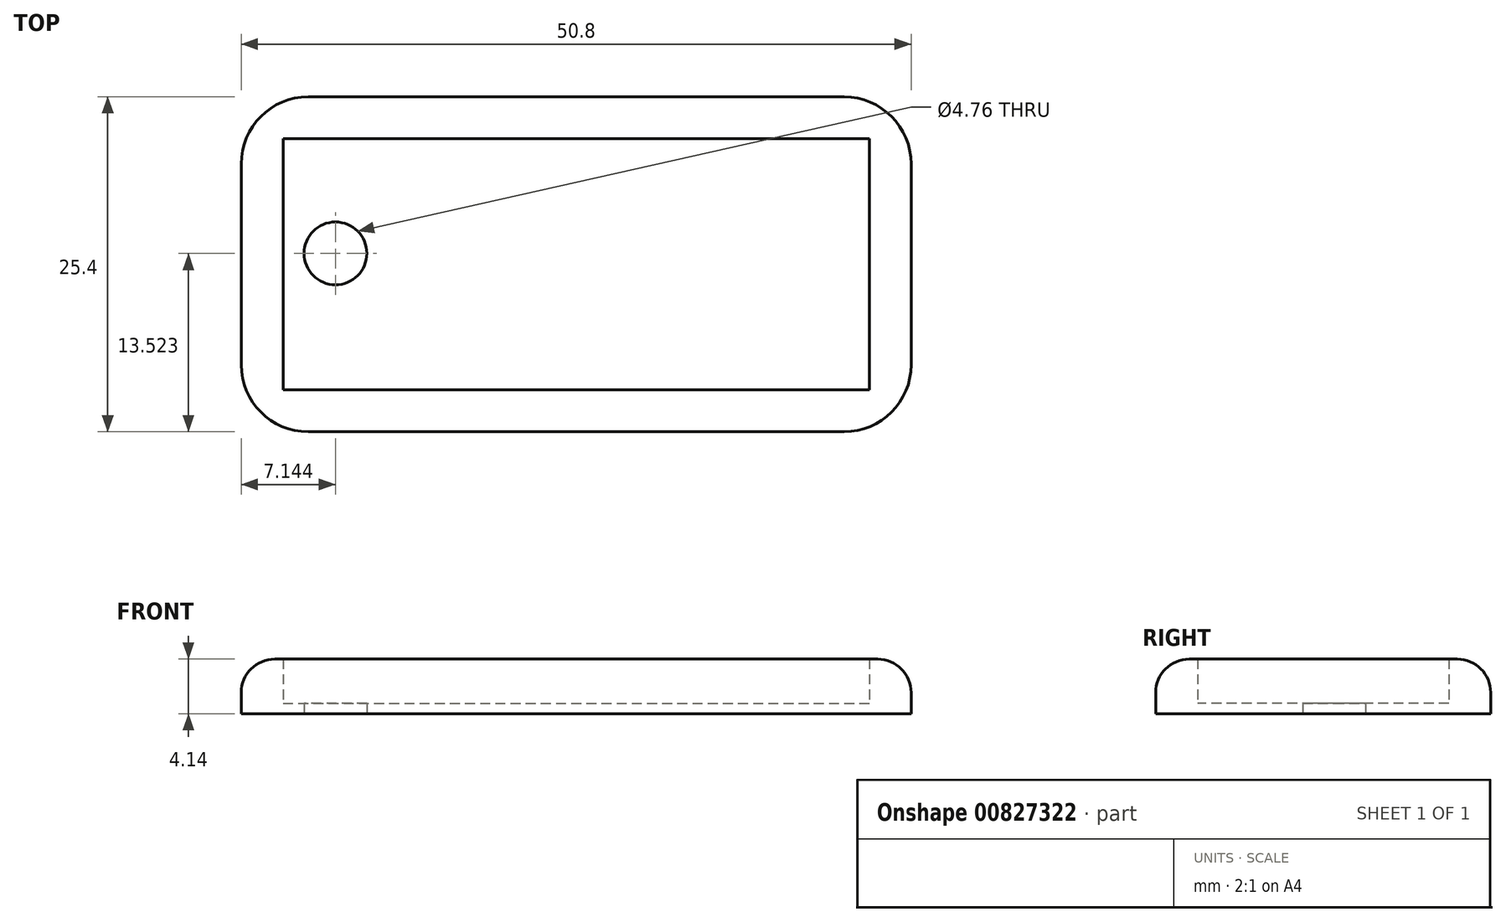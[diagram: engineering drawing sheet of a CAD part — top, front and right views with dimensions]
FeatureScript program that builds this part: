
annotation { "Feature Type Name" : "Feature", "Feature Type Description" : "" }
export const myFeature = defineFeature(function(context is Context, id is Id, definition is map)
    precondition{}
    {
        {
            var Q0;
            Q0=qCreatedBy(makeId("Top.planeOp"),FACE);
            var sketch = newSketch(context, id + "F0", { "sketchPlane" : qUnion([Q0])});
            skLineSegment(sketch, "E0.bottom", {"start": v(0, 0) * mm, "end": v(0, 0) * mm});
            skLineSegment(sketch, "E0.top", {"start": v(0, 23.75) * mm, "end": v(0, 23.75) * mm});
            skLineSegment(sketch, "E0.left", {"start": v(0, 0) * mm, "end": v(0, 23.75) * mm});
            skLineSegment(sketch, "E0.right", {"start": v(0, 0) * mm, "end": v(0, 23.75) * mm});
            skLineSegment(sketch, "E1.bottom", {"start": v(0, 23.75) * mm, "end": v(50.8, 23.75) * mm});
            skLineSegment(sketch, "E1.top", {"start": v(0, -1.65) * mm, "end": v(50.8, -1.65) * mm});
            skLineSegment(sketch, "E1.left", {"start": v(0, 23.75) * mm, "end": v(0, -1.65) * mm});
            skLineSegment(sketch, "E1.right", {"start": v(50.8, 23.75) * mm, "end": v(50.8, -1.65) * mm});
            skCircle(sketch, "E2", {"center": v(7.14, 11.87) * mm, "radius": 2.38 * mm});
            skPoint(sketch, "E2.centerSnap0", {"position": v(0, 11.87) * mm});
            skLineSegment(sketch, "E3.bottom", {"start": v(3.18, 20.57) * mm, "end": v(47.63, 20.57) * mm});
            skLineSegment(sketch, "E3.top", {"start": v(3.18, 1.52) * mm, "end": v(47.63, 1.52) * mm});
            skLineSegment(sketch, "E3.left", {"start": v(3.17, 20.57) * mm, "end": v(3.18, 1.52) * mm});
            skLineSegment(sketch, "E3.right", {"start": v(47.63, 20.57) * mm, "end": v(47.63, 1.52) * mm});
            skSolve(sketch);
        }
        {
            var Q0;
            Q0=makeQuery(id+"F0.imprint","IMPRINT",FACE,{"disambiguationData":[TD([[makeQuery(id+"F0.imprint","IMPRINT",EDGE,{"derivedFrom":sQuery(id+"F0.wireOp",EDGE,"E2")}),-1.0]])]});
            extrude(context, id + "F1", {"entities" : qUnion([Q0]), "depth" : 0.8 * mm, "offsetDistance" : 25.4 * mm});
        }
        {
            var Q0;
            Q0 = qSketchRegion(id + "F0", true);
            extrude(context, id + "F2", {"entities" : qUnion([Q0]), "operationType" : NewBodyOperationType.ADD, "depth" : 4.14 * mm, "offsetDistance" : 25.4 * mm});
        }
        {
            var Q0;
            Q0=makeQuery(id+"F2.opExtrude","SWEPT_EDGE",EDGE,{"disambiguationData":[OSD([sQuery(id+"F0.wireOp",EDGE,"E1.top"),sQuery(id+"F0.wireOp",EDGE,"E1.right")])]});
            var Q1;
            Q1=makeQuery(id+"F2.opExtrude","SWEPT_EDGE",EDGE,{"disambiguationData":[OSD([sQuery(id+"F0.wireOp",EDGE,"E1.top"),sQuery(id+"F0.wireOp",EDGE,"E1.left")])]});
            var Q2;
            Q2=makeQuery(id+"F2.opExtrude","SWEPT_EDGE",EDGE,{"disambiguationData":[OSD([sQuery(id+"F0.wireOp",EDGE,"E1.bottom"),sQuery(id+"F0.wireOp",EDGE,"E1.right")])]});
            var Q3;
            Q3=makeQuery(id+"F2.opExtrude","SWEPT_EDGE",EDGE,{"disambiguationData":[OSD([sQuery(id+"F0.wireOp",EDGE,"E1.bottom"),sQuery(id+"F0.wireOp",EDGE,"E1.left")])]});
            fillet(context, id + "F3", {"entities" : qUnion([Q0, Q1, Q2, Q3]), "radius" : 5.08 * mm, "tangentPropagation" : true, "allowEdgeOverflow" : false});
        }
        {
            var Q0;
            Q0=makeQuery(id+"F2.opExtrude","CAP_EDGE",EDGE,{"disambiguationData":[OSD([sQuery(id+"F0.wireOp",EDGE,"E1.top")])],"isStart":false});
            fillet(context, id + "F4", {"entities" : qUnion([Q0]), "radius" : 2.54 * mm, "tangentPropagation" : true, "allowEdgeOverflow" : false});
        }
    });
